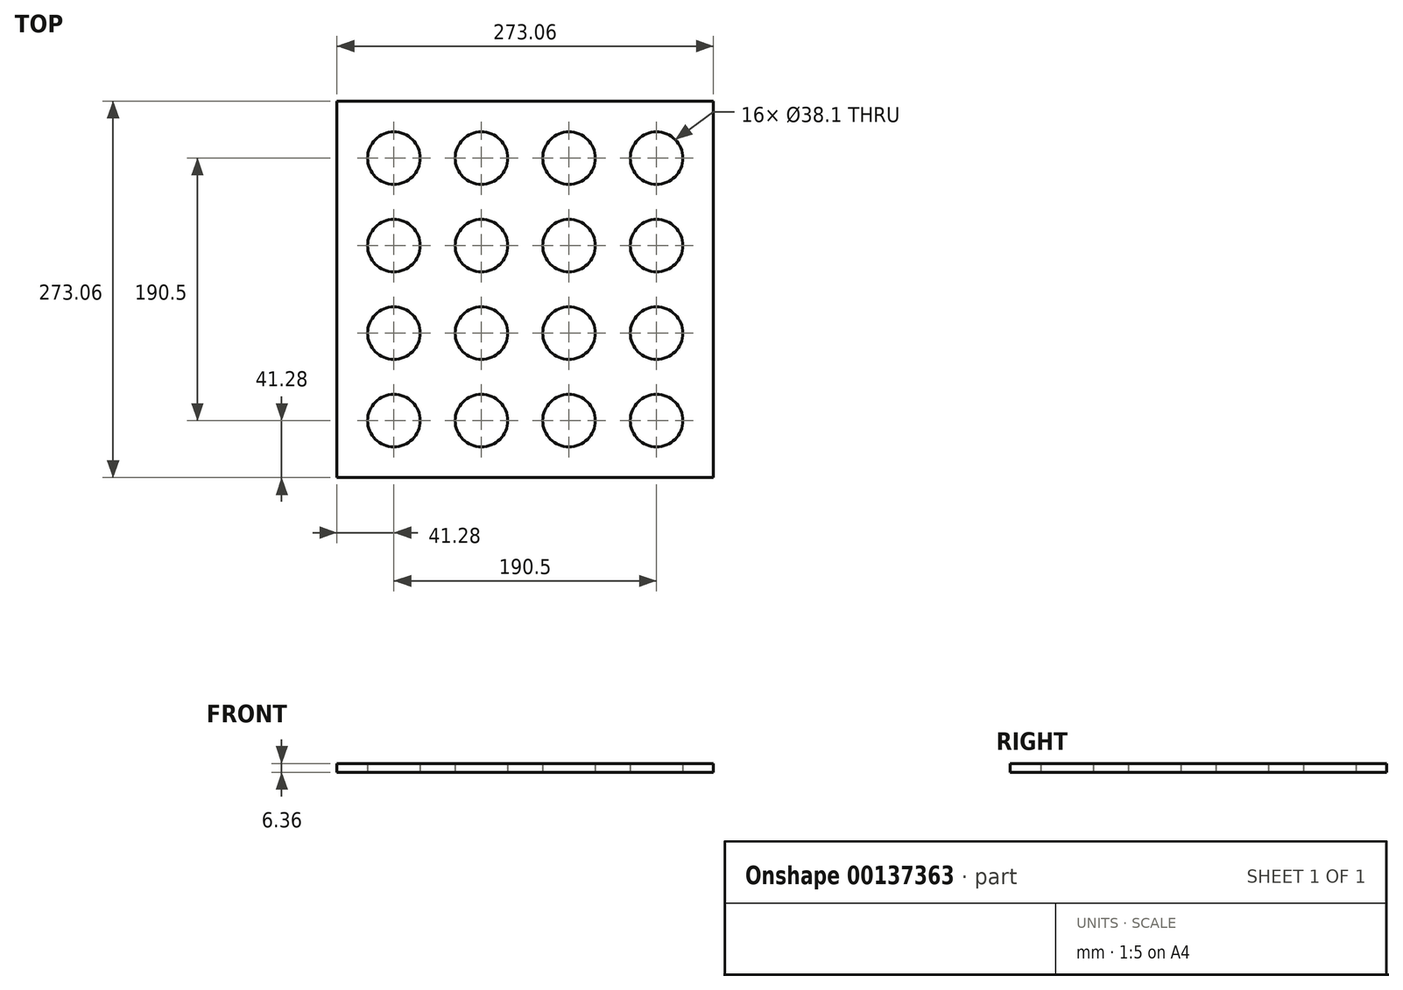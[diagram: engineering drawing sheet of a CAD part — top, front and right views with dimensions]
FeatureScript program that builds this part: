
annotation { "Feature Type Name" : "Feature", "Feature Type Description" : "" }
export const myFeature = defineFeature(function(context is Context, id is Id, definition is map)
    precondition{}
    {
        {
            var Q0;
            Q0=qCreatedBy(makeId("Top.planeOp"),FACE);
            var sketch = newSketch(context, id + "F0", { "sketchPlane" : qUnion([Q0])});
            skLineSegment(sketch, "E0.bottom", {"start": v(-136.52, 136.53) * mm, "end": v(136.53, 136.53) * mm});
            skLineSegment(sketch, "E0.top", {"start": v(-136.53, -136.53) * mm, "end": v(136.52, -136.53) * mm});
            skLineSegment(sketch, "E0.left", {"start": v(-136.52, 136.53) * mm, "end": v(-136.53, -136.52) * mm});
            skLineSegment(sketch, "E0.right", {"start": v(136.53, 136.53) * mm, "end": v(136.52, -136.52) * mm});
            skPoint(sketch, "E0.middle", {"position": v(0, 0) * mm});
            skCircle(sketch, "E1", {"center": v(-95.25, 95.25) * mm, "radius": 19.05 * mm});
            skCircle(sketch, "E2.0.1.0", {"center": v(-95.25, 31.75) * mm, "radius": 19.05 * mm});
            skCircle(sketch, "E2.0.2.0", {"center": v(-95.25, -31.75) * mm, "radius": 19.05 * mm});
            skCircle(sketch, "E2.0.3.0", {"center": v(-95.25, -95.25) * mm, "radius": 19.05 * mm});
            skCircle(sketch, "E2.1.0.0", {"center": v(-31.75, 95.25) * mm, "radius": 19.05 * mm});
            skCircle(sketch, "E2.1.1.0", {"center": v(-31.75, 31.75) * mm, "radius": 19.05 * mm});
            skCircle(sketch, "E2.1.2.0", {"center": v(-31.75, -31.75) * mm, "radius": 19.05 * mm});
            skCircle(sketch, "E2.1.3.0", {"center": v(-31.75, -95.25) * mm, "radius": 19.05 * mm});
            skCircle(sketch, "E2.2.0.0", {"center": v(31.75, 95.25) * mm, "radius": 19.05 * mm});
            skCircle(sketch, "E2.2.1.0", {"center": v(31.75, 31.75) * mm, "radius": 19.05 * mm});
            skCircle(sketch, "E2.2.2.0", {"center": v(31.75, -31.75) * mm, "radius": 19.05 * mm});
            skCircle(sketch, "E2.2.3.0", {"center": v(31.75, -95.25) * mm, "radius": 19.05 * mm});
            skCircle(sketch, "E2.3.0.0", {"center": v(95.25, 95.25) * mm, "radius": 19.05 * mm});
            skCircle(sketch, "E2.3.1.0", {"center": v(95.25, 31.75) * mm, "radius": 19.05 * mm});
            skCircle(sketch, "E2.3.2.0", {"center": v(95.25, -31.75) * mm, "radius": 19.05 * mm});
            skCircle(sketch, "E2.3.3.0", {"center": v(95.25, -95.25) * mm, "radius": 19.05 * mm});
            skLineSegment(sketch, "E2.direction1", {"start": v(-95.25, 95.25) * mm, "end": v(-31.75, 95.25) * mm, "construction": true});
            skLineSegment(sketch, "E2.direction2", {"start": v(-95.25, 95.25) * mm, "end": v(-95.25, 31.75) * mm, "construction": true});
            skSolve(sketch);
        }
        {
            var Q0;
            Q0=makeQuery(id+"F0.imprint","IMPRINT",FACE,{"disambiguationData":[TD([[makeQuery(id+"F0.imprint","IMPRINT",EDGE,{"derivedFrom":sQuery(id+"F0.wireOp",EDGE,"E0.bottom")}),-1.0]])]});
            extrude(context, id + "F1", {"entities" : qUnion([Q0]), "endBound" : BoundingType.SYMMETRIC, "depth" : 6.35 * mm});
        }
    });
